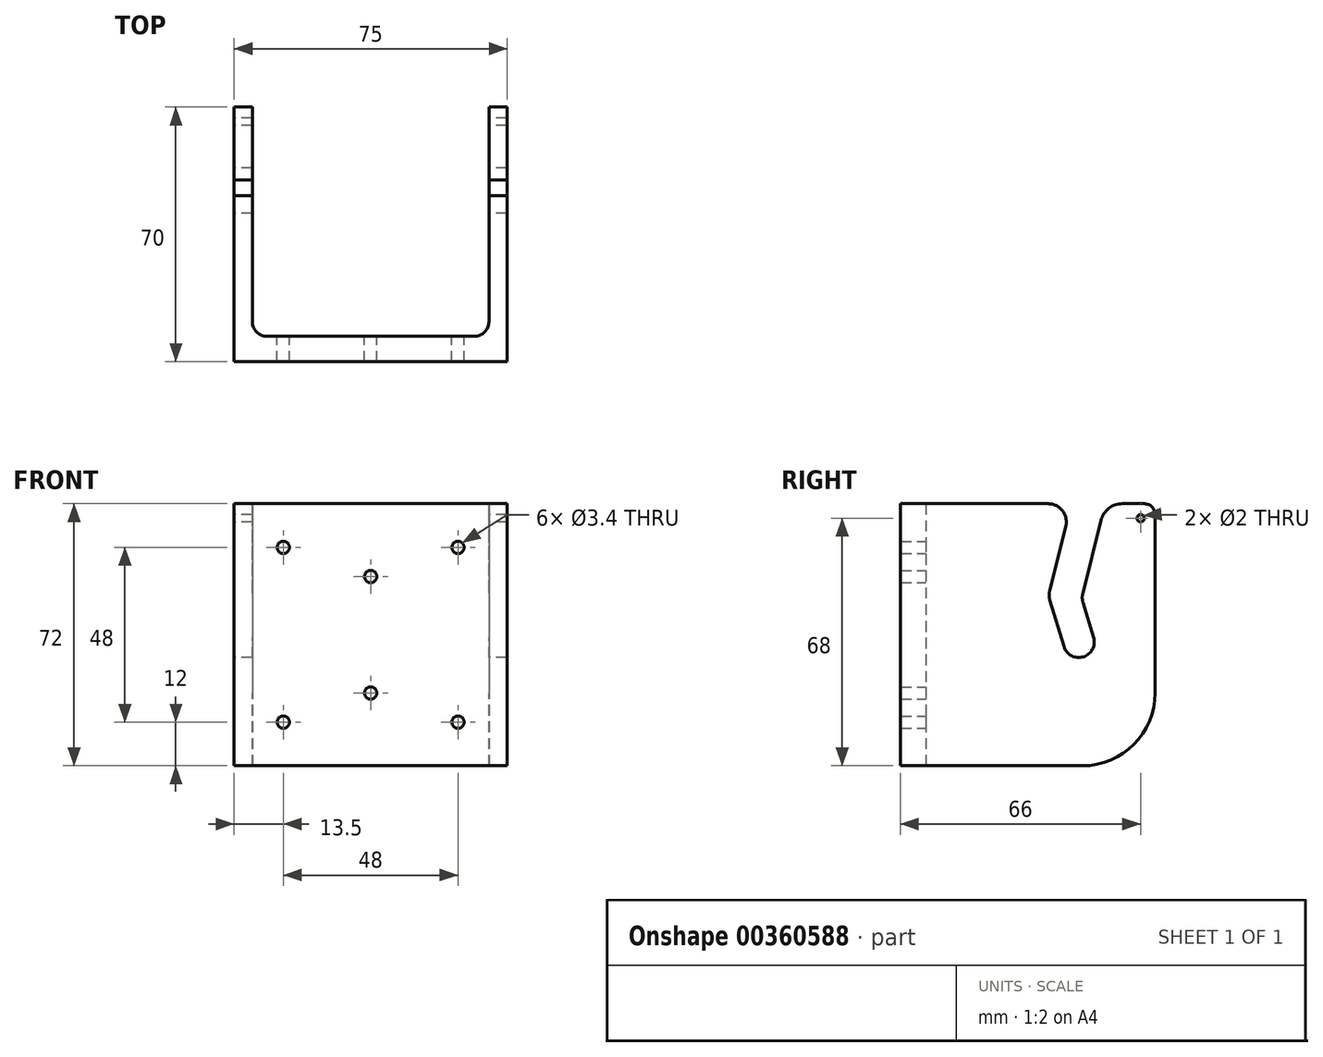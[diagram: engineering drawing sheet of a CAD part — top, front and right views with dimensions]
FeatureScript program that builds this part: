
annotation { "Feature Type Name" : "Feature", "Feature Type Description" : "" }
export const myFeature = defineFeature(function(context is Context, id is Id, definition is map)
    precondition{}
    {
        {
            var Q0;
            Q0=qCreatedBy(makeId("Right.planeOp"),FACE);
            var sketch = newSketch(context, id + "F0", { "sketchPlane" : qUnion([Q0])});
            skLineSegment(sketch, "E0.bottom", {"start": v(0, 0) * mm, "end": v(50, 0) * mm});
            skLineSegment(sketch, "E0.left", {"start": v(0, 0) * mm, "end": v(0, 72) * mm});
            skLineSegment(sketch, "E0.right", {"start": v(70, 20) * mm, "end": v(70, 69) * mm});
            skLineSegment(sketch, "E1", {"start": v(49, 34) * mm, "end": v(0, 34) * mm, "construction": true});
            skCircle(sketch, "E2", {"center": v(66, 68) * mm, "radius": 1 * mm});
            skPoint(sketch, "E3.visualSharp", {"position": v(70, 0) * mm});
            skArc(sketch, "E3.filletArc", {"start": v(50, 0) * mm, "mid": v(64.14, 5.86) * mm, "end": v(70, 20) * mm});
            skPoint(sketch, "E4.visualSharp", {"position": v(70, 70) * mm});
            skArc(sketch, "E4.filletArc", {"start": v(70, 69) * mm, "mid": v(69.12, 71.12) * mm, "end": v(67, 72) * mm});
            skLineSegment(sketch, "E5", {"start": v(67, 72) * mm, "end": v(60.96, 72) * mm});
            skArc(sketch, "E6", {"start": v(44.93, 32.76) * mm, "mid": v(50.23, 29.93) * mm, "end": v(53.07, 35.22) * mm});
            skLineSegment(sketch, "E7", {"start": v(41.07, 45.47) * mm, "end": v(44.93, 32.76) * mm});
            skLineSegment(sketch, "E8", {"start": v(50.18, 44.82) * mm, "end": v(53.07, 35.22) * mm});
            skLineSegment(sketch, "E9", {"start": v(41, 48.14) * mm, "end": v(45.44, 65.78) * mm});
            skLineSegment(sketch, "E10", {"start": v(50.12, 47.48) * mm, "end": v(55.14, 67.46) * mm});
            skPoint(sketch, "E11.orphan", {"position": v(33, 72) * mm});
            skPoint(sketch, "E12.orphan", {"position": v(42, 72) * mm});
            skLineSegment(sketch, "E13.trimOffspring", {"start": v(40.59, 72) * mm, "end": v(0, 72) * mm});
            skPoint(sketch, "E14.visualSharp", {"position": v(40.67, 46.8) * mm});
            skArc(sketch, "E14.filletArc", {"start": v(41, 48.14) * mm, "mid": v(40.85, 46.8) * mm, "end": v(41.07, 45.47) * mm});
            skPoint(sketch, "E15.visualSharp", {"position": v(49.78, 46.15) * mm});
            skArc(sketch, "E15.filletArc", {"start": v(50.12, 47.48) * mm, "mid": v(49.97, 46.15) * mm, "end": v(50.18, 44.82) * mm});
            skPoint(sketch, "E16.visualSharp", {"position": v(56.28, 72) * mm});
            skArc(sketch, "E16.filletArc", {"start": v(60.96, 72) * mm, "mid": v(57.27, 70.73) * mm, "end": v(55.14, 67.46) * mm});
            skPoint(sketch, "E17.visualSharp", {"position": v(47, 72) * mm});
            skArc(sketch, "E17.filletArc", {"start": v(45.44, 65.78) * mm, "mid": v(44.53, 70.07) * mm, "end": v(40.59, 72) * mm});
            skCircle(sketch, "E18", {"center": v(49, 34) * mm, "radius": 33 * mm, "construction": true});
            skSolve(sketch);
        }
        {
            var Q0;
            Q0 = qSketchRegion(id + "F0", true);
            extrude(context, id + "F1", {"entities" : qUnion([Q0]), "depth" : 75 * mm});
        }
        {
            var Q0;
            Q0=makeQuery(id+"F1.opExtrude","SWEPT_FACE",FACE,{"disambiguationData":[OSD([sQuery(id+"F0.wireOp",EDGE,"E0.right")])]});
            var sketch = newSketch(context, id + "F2", { "sketchPlane" : qUnion([Q0])});
            skLineSegment(sketch, "E19.left", {"start": v(-70, 89.13) * mm, "end": v(-70, -5.87) * mm});
            skLineSegment(sketch, "E20", {"start": v(-37.5, 20) * mm, "end": v(-37.5, 82.42) * mm, "construction": true});
            skLineSegment(sketch, "E21.MirrorCS", {"start": v(-5, 89.13) * mm, "end": v(-5, -5.87) * mm});
            skLineSegment(sketch, "E22", {"start": v(-70, 89.13) * mm, "end": v(-5, 89.13) * mm});
            skLineSegment(sketch, "E23", {"start": v(-5, -5.87) * mm, "end": v(-70, -5.87) * mm});
            skSolve(sketch);
        }
        {
            var Q0;
            Q0 = qSketchRegion(id + "F2", true);
            extrude(context, id + "F3", {"entities" : qUnion([Q0]), "operationType" : NewBodyOperationType.REMOVE, "oppositeDirection" : true, "depth" : 63 * mm});
        }
        {
            var Q0;
            Q0=makeQuery(id+"F3.boolean.opBoolean","COPY",FACE,{"derivedFrom":makeQuery(id+"F3.opExtrude","CAP_FACE",FACE,{"disambiguationData":[OSD([sQuery(id+"F2.wireOp",EDGE,"E19.left"),sQuery(id+"F2.wireOp",EDGE,"E21.MirrorCS"),sQuery(id+"F2.wireOp",EDGE,"E22"),sQuery(id+"F2.wireOp",EDGE,"E23")])],"isStart":false})});
            var sketch = newSketch(context, id + "F4", { "sketchPlane" : qUnion([Q0])});
            skLineSegment(sketch, "E24", {"start": v(-37.5, 72) * mm, "end": v(-37.5, 0) * mm, "construction": true});
            skLineSegment(sketch, "E25", {"start": v(-37.5, 36) * mm, "end": v(-91, 36) * mm, "construction": true});
            skPoint(sketch, "E25.endSnap0", {"position": v(-70, 36) * mm});
            skCircle(sketch, "E26", {"center": v(-61.5, 60) * mm, "radius": 1.7 * mm});
            skCircle(sketch, "E27", {"center": v(-61.5, 12) * mm, "radius": 1.7 * mm});
            skCircle(sketch, "E28.MirrorC", {"center": v(-13.5, 12) * mm, "radius": 1.7 * mm});
            skCircle(sketch, "E29.MirrorC", {"center": v(-13.5, 60) * mm, "radius": 1.7 * mm});
            skCircle(sketch, "E30", {"center": v(-37.5, 52) * mm, "radius": 1.7 * mm});
            skCircle(sketch, "E31.MirrorC", {"center": v(-37.5, 20) * mm, "radius": 1.7 * mm});
            skSolve(sketch);
        }
        {
            var Q0;
            Q0 = qSketchRegion(id + "F4", true);
            extrude(context, id + "F5", {"entities" : qUnion([Q0]), "operationType" : NewBodyOperationType.REMOVE, "endBound" : BoundingType.THROUGH_ALL, "oppositeDirection" : true, "depth" : 25 * mm});
        }
        {
            var Q0;
            Q0=makeQuery(id+"F3.boolean.opBoolean","COPY",EDGE,{"derivedFrom":makeQuery(id+"F3.opExtrude","CAP_EDGE",EDGE,{"disambiguationData":[OSD([sQuery(id+"F2.wireOp",EDGE,"E19.left")])],"isStart":false})});
            var Q1;
            Q1=makeQuery(id+"F3.boolean.opBoolean","COPY",EDGE,{"derivedFrom":makeQuery(id+"F3.opExtrude","CAP_EDGE",EDGE,{"disambiguationData":[OSD([sQuery(id+"F2.wireOp",EDGE,"E21.MirrorCS")])],"isStart":false})});
            fillet(context, id + "F6", {"entities" : qUnion([Q0, Q1]), "radius" : 4 * mm, "tangentPropagation" : true, "allowEdgeOverflow" : false});
        }
    });
